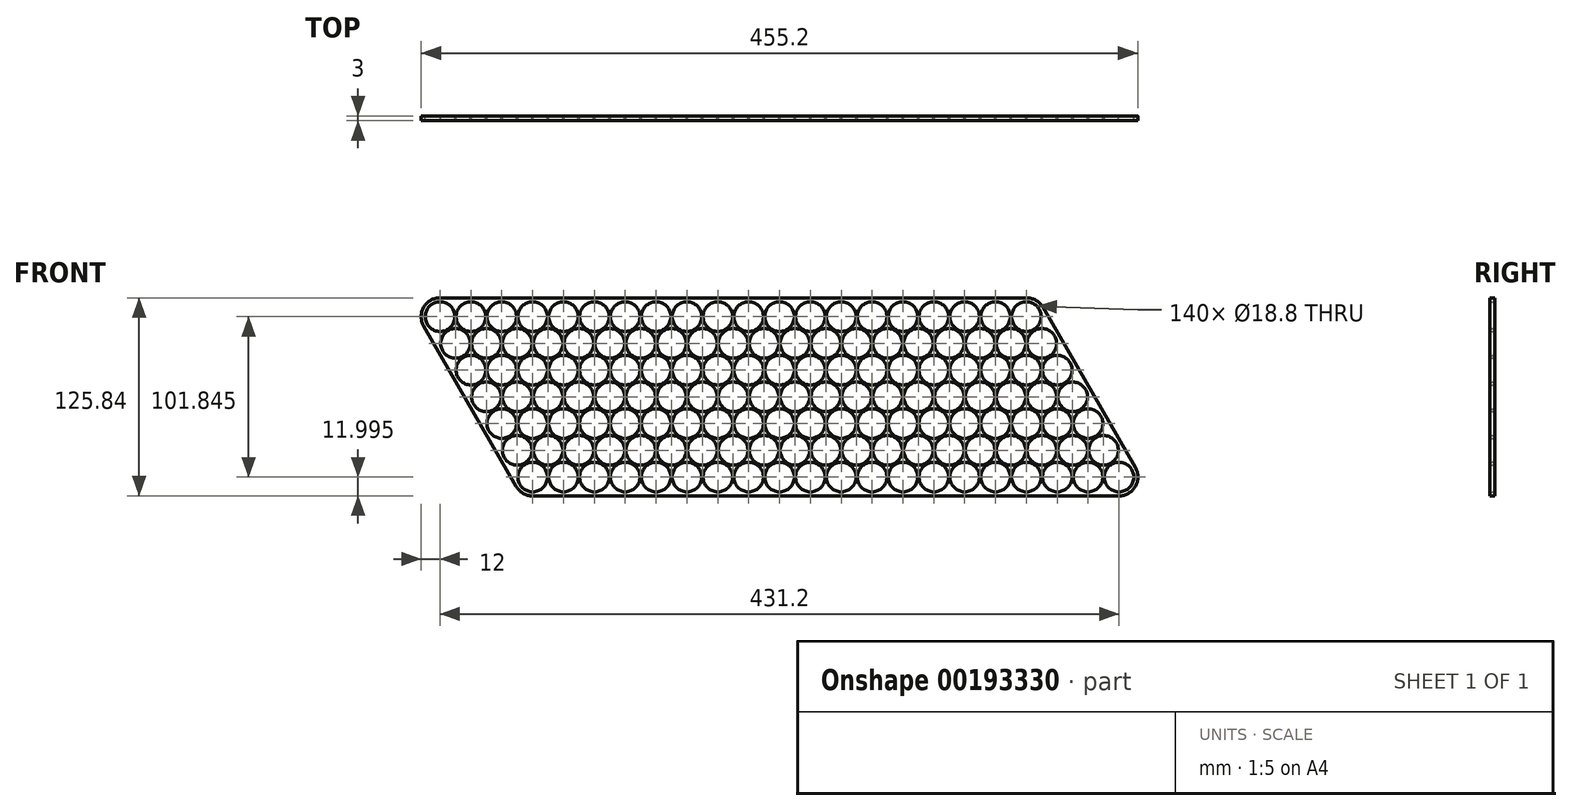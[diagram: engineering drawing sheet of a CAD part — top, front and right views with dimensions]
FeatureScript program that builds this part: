
annotation { "Feature Type Name" : "Feature", "Feature Type Description" : "" }
export const myFeature = defineFeature(function(context is Context, id is Id, definition is map)
    precondition{}
    {
        {
            var Q0;
            Q0=qCreatedBy(makeId("Front.planeOp"),FACE);
            var sketch = newSketch(context, id + "F0", { "sketchPlane" : qUnion([Q0])});
            skLineSegment(sketch, "E0", {"start": v(0, 0) * mm, "end": v(79.44, 0) * mm, "construction": true});
            skLineSegment(sketch, "E1", {"start": v(0, 0) * mm, "end": v(43.4, -75.16) * mm, "construction": true});
            skCircle(sketch, "E2", {"center": v(0, 0) * mm, "radius": 9.4 * mm});
            skCircle(sketch, "E3.1.0.0", {"center": v(19.6, 0) * mm, "radius": 9.4 * mm});
            skCircle(sketch, "E3.2.0.0", {"center": v(39.2, 0) * mm, "radius": 9.4 * mm});
            skCircle(sketch, "E3.3.0.0", {"center": v(58.8, 0) * mm, "radius": 9.4 * mm});
            skCircle(sketch, "E3.4.0.0", {"center": v(78.4, 0) * mm, "radius": 9.4 * mm});
            skCircle(sketch, "E3.5.0.0", {"center": v(98, 0) * mm, "radius": 9.4 * mm});
            skCircle(sketch, "E3.6.0.0", {"center": v(117.6, 0) * mm, "radius": 9.4 * mm});
            skCircle(sketch, "E3.7.0.0", {"center": v(137.2, 0) * mm, "radius": 9.4 * mm});
            skCircle(sketch, "E3.8.0.0", {"center": v(156.8, 0) * mm, "radius": 9.4 * mm});
            skCircle(sketch, "E3.9.0.0", {"center": v(176.4, 0) * mm, "radius": 9.4 * mm});
            skCircle(sketch, "E3.10.0.0", {"center": v(196, 0) * mm, "radius": 9.4 * mm});
            skCircle(sketch, "E3.11.0.0", {"center": v(215.6, 0) * mm, "radius": 9.4 * mm});
            skCircle(sketch, "E3.12.0.0", {"center": v(235.2, 0) * mm, "radius": 9.4 * mm});
            skCircle(sketch, "E3.13.0.0", {"center": v(254.8, 0) * mm, "radius": 9.4 * mm});
            skCircle(sketch, "E3.14.0.0", {"center": v(274.4, 0) * mm, "radius": 9.4 * mm});
            skCircle(sketch, "E3.15.0.0", {"center": v(294, 0) * mm, "radius": 9.4 * mm});
            skCircle(sketch, "E3.16.0.0", {"center": v(313.6, 0) * mm, "radius": 9.4 * mm});
            skCircle(sketch, "E3.17.0.0", {"center": v(333.2, 0) * mm, "radius": 9.4 * mm});
            skCircle(sketch, "E3.18.0.0", {"center": v(352.8, 0) * mm, "radius": 9.4 * mm});
            skCircle(sketch, "E3.19.0.0", {"center": v(372.4, 0) * mm, "radius": 9.4 * mm});
            skLineSegment(sketch, "E3.direction1", {"start": v(0, 0) * mm, "end": v(19.6, 0) * mm, "construction": true});
            skCircle(sketch, "E4.1.0.0", {"center": v(9.8, -16.97) * mm, "radius": 9.4 * mm});
            skCircle(sketch, "E4.2.0.0", {"center": v(19.6, -33.95) * mm, "radius": 9.4 * mm});
            skCircle(sketch, "E4.3.0.0", {"center": v(29.4, -50.92) * mm, "radius": 9.4 * mm});
            skCircle(sketch, "E4.4.0.0", {"center": v(39.2, -67.9) * mm, "radius": 9.4 * mm});
            skCircle(sketch, "E4.5.0.0", {"center": v(49, -84.87) * mm, "radius": 9.4 * mm});
            skCircle(sketch, "E4.6.0.0", {"center": v(58.8, -101.84) * mm, "radius": 9.4 * mm});
            skLineSegment(sketch, "E4.direction1", {"start": v(0, 0) * mm, "end": v(9.8, -16.97) * mm, "construction": true});
            skCircle(sketch, "E5.1.0.0", {"center": v(29.4, -16.97) * mm, "radius": 9.4 * mm});
            skCircle(sketch, "E5.1.0.1", {"center": v(39.2, -33.95) * mm, "radius": 9.4 * mm});
            skCircle(sketch, "E5.1.0.2", {"center": v(49, -50.92) * mm, "radius": 9.4 * mm});
            skCircle(sketch, "E5.1.0.3", {"center": v(58.8, -67.9) * mm, "radius": 9.4 * mm});
            skCircle(sketch, "E5.1.0.4", {"center": v(68.6, -84.87) * mm, "radius": 9.4 * mm});
            skCircle(sketch, "E5.1.0.5", {"center": v(78.4, -101.84) * mm, "radius": 9.4 * mm});
            skCircle(sketch, "E5.2.0.0", {"center": v(49, -16.97) * mm, "radius": 9.4 * mm});
            skCircle(sketch, "E5.2.0.1", {"center": v(58.8, -33.95) * mm, "radius": 9.4 * mm});
            skCircle(sketch, "E5.2.0.2", {"center": v(68.6, -50.92) * mm, "radius": 9.4 * mm});
            skCircle(sketch, "E5.2.0.3", {"center": v(78.4, -67.9) * mm, "radius": 9.4 * mm});
            skCircle(sketch, "E5.2.0.4", {"center": v(88.2, -84.87) * mm, "radius": 9.4 * mm});
            skCircle(sketch, "E5.2.0.5", {"center": v(98, -101.84) * mm, "radius": 9.4 * mm});
            skCircle(sketch, "E5.3.0.0", {"center": v(68.6, -16.97) * mm, "radius": 9.4 * mm});
            skCircle(sketch, "E5.3.0.1", {"center": v(78.4, -33.95) * mm, "radius": 9.4 * mm});
            skCircle(sketch, "E5.3.0.2", {"center": v(88.2, -50.92) * mm, "radius": 9.4 * mm});
            skCircle(sketch, "E5.3.0.3", {"center": v(98, -67.9) * mm, "radius": 9.4 * mm});
            skCircle(sketch, "E5.3.0.4", {"center": v(107.8, -84.87) * mm, "radius": 9.4 * mm});
            skCircle(sketch, "E5.3.0.5", {"center": v(117.6, -101.84) * mm, "radius": 9.4 * mm});
            skCircle(sketch, "E5.4.0.0", {"center": v(88.2, -16.97) * mm, "radius": 9.4 * mm});
            skCircle(sketch, "E5.4.0.1", {"center": v(98, -33.95) * mm, "radius": 9.4 * mm});
            skCircle(sketch, "E5.4.0.2", {"center": v(107.8, -50.92) * mm, "radius": 9.4 * mm});
            skCircle(sketch, "E5.4.0.3", {"center": v(117.6, -67.9) * mm, "radius": 9.4 * mm});
            skCircle(sketch, "E5.4.0.4", {"center": v(127.4, -84.87) * mm, "radius": 9.4 * mm});
            skCircle(sketch, "E5.4.0.5", {"center": v(137.2, -101.84) * mm, "radius": 9.4 * mm});
            skCircle(sketch, "E5.5.0.0", {"center": v(107.8, -16.97) * mm, "radius": 9.4 * mm});
            skCircle(sketch, "E5.5.0.1", {"center": v(117.6, -33.95) * mm, "radius": 9.4 * mm});
            skCircle(sketch, "E5.5.0.2", {"center": v(127.4, -50.92) * mm, "radius": 9.4 * mm});
            skCircle(sketch, "E5.5.0.3", {"center": v(137.2, -67.9) * mm, "radius": 9.4 * mm});
            skCircle(sketch, "E5.5.0.4", {"center": v(147, -84.87) * mm, "radius": 9.4 * mm});
            skCircle(sketch, "E5.5.0.5", {"center": v(156.8, -101.84) * mm, "radius": 9.4 * mm});
            skCircle(sketch, "E5.6.0.0", {"center": v(127.4, -16.97) * mm, "radius": 9.4 * mm});
            skCircle(sketch, "E5.6.0.1", {"center": v(137.2, -33.95) * mm, "radius": 9.4 * mm});
            skCircle(sketch, "E5.6.0.2", {"center": v(147, -50.92) * mm, "radius": 9.4 * mm});
            skCircle(sketch, "E5.6.0.3", {"center": v(156.8, -67.9) * mm, "radius": 9.4 * mm});
            skCircle(sketch, "E5.6.0.4", {"center": v(166.6, -84.87) * mm, "radius": 9.4 * mm});
            skCircle(sketch, "E5.6.0.5", {"center": v(176.4, -101.84) * mm, "radius": 9.4 * mm});
            skCircle(sketch, "E5.7.0.0", {"center": v(147, -16.97) * mm, "radius": 9.4 * mm});
            skCircle(sketch, "E5.7.0.1", {"center": v(156.8, -33.95) * mm, "radius": 9.4 * mm});
            skCircle(sketch, "E5.7.0.2", {"center": v(166.6, -50.92) * mm, "radius": 9.4 * mm});
            skCircle(sketch, "E5.7.0.3", {"center": v(176.4, -67.9) * mm, "radius": 9.4 * mm});
            skCircle(sketch, "E5.7.0.4", {"center": v(186.2, -84.87) * mm, "radius": 9.4 * mm});
            skCircle(sketch, "E5.7.0.5", {"center": v(196, -101.84) * mm, "radius": 9.4 * mm});
            skCircle(sketch, "E5.8.0.0", {"center": v(166.6, -16.97) * mm, "radius": 9.4 * mm});
            skCircle(sketch, "E5.8.0.1", {"center": v(176.4, -33.95) * mm, "radius": 9.4 * mm});
            skCircle(sketch, "E5.8.0.2", {"center": v(186.2, -50.92) * mm, "radius": 9.4 * mm});
            skCircle(sketch, "E5.8.0.3", {"center": v(196, -67.9) * mm, "radius": 9.4 * mm});
            skCircle(sketch, "E5.8.0.4", {"center": v(205.8, -84.87) * mm, "radius": 9.4 * mm});
            skCircle(sketch, "E5.8.0.5", {"center": v(215.6, -101.84) * mm, "radius": 9.4 * mm});
            skCircle(sketch, "E5.9.0.0", {"center": v(186.2, -16.97) * mm, "radius": 9.4 * mm});
            skCircle(sketch, "E5.9.0.1", {"center": v(196, -33.95) * mm, "radius": 9.4 * mm});
            skCircle(sketch, "E5.9.0.2", {"center": v(205.8, -50.92) * mm, "radius": 9.4 * mm});
            skCircle(sketch, "E5.9.0.3", {"center": v(215.6, -67.9) * mm, "radius": 9.4 * mm});
            skCircle(sketch, "E5.9.0.4", {"center": v(225.4, -84.87) * mm, "radius": 9.4 * mm});
            skCircle(sketch, "E5.9.0.5", {"center": v(235.2, -101.84) * mm, "radius": 9.4 * mm});
            skCircle(sketch, "E5.10.0.0", {"center": v(205.8, -16.97) * mm, "radius": 9.4 * mm});
            skCircle(sketch, "E5.10.0.1", {"center": v(215.6, -33.95) * mm, "radius": 9.4 * mm});
            skCircle(sketch, "E5.10.0.2", {"center": v(225.4, -50.92) * mm, "radius": 9.4 * mm});
            skCircle(sketch, "E5.10.0.3", {"center": v(235.2, -67.9) * mm, "radius": 9.4 * mm});
            skCircle(sketch, "E5.10.0.4", {"center": v(245, -84.87) * mm, "radius": 9.4 * mm});
            skCircle(sketch, "E5.10.0.5", {"center": v(254.8, -101.84) * mm, "radius": 9.4 * mm});
            skCircle(sketch, "E5.11.0.0", {"center": v(225.4, -16.97) * mm, "radius": 9.4 * mm});
            skCircle(sketch, "E5.11.0.1", {"center": v(235.2, -33.95) * mm, "radius": 9.4 * mm});
            skCircle(sketch, "E5.11.0.2", {"center": v(245, -50.92) * mm, "radius": 9.4 * mm});
            skCircle(sketch, "E5.11.0.3", {"center": v(254.8, -67.9) * mm, "radius": 9.4 * mm});
            skCircle(sketch, "E5.11.0.4", {"center": v(264.6, -84.87) * mm, "radius": 9.4 * mm});
            skCircle(sketch, "E5.11.0.5", {"center": v(274.4, -101.84) * mm, "radius": 9.4 * mm});
            skCircle(sketch, "E5.12.0.0", {"center": v(245, -16.97) * mm, "radius": 9.4 * mm});
            skCircle(sketch, "E5.12.0.1", {"center": v(254.8, -33.95) * mm, "radius": 9.4 * mm});
            skCircle(sketch, "E5.12.0.2", {"center": v(264.6, -50.92) * mm, "radius": 9.4 * mm});
            skCircle(sketch, "E5.12.0.3", {"center": v(274.4, -67.9) * mm, "radius": 9.4 * mm});
            skCircle(sketch, "E5.12.0.4", {"center": v(284.2, -84.87) * mm, "radius": 9.4 * mm});
            skCircle(sketch, "E5.12.0.5", {"center": v(294, -101.84) * mm, "radius": 9.4 * mm});
            skCircle(sketch, "E5.13.0.0", {"center": v(264.6, -16.97) * mm, "radius": 9.4 * mm});
            skCircle(sketch, "E5.13.0.1", {"center": v(274.4, -33.95) * mm, "radius": 9.4 * mm});
            skCircle(sketch, "E5.13.0.2", {"center": v(284.2, -50.92) * mm, "radius": 9.4 * mm});
            skCircle(sketch, "E5.13.0.3", {"center": v(294, -67.9) * mm, "radius": 9.4 * mm});
            skCircle(sketch, "E5.13.0.4", {"center": v(303.8, -84.87) * mm, "radius": 9.4 * mm});
            skCircle(sketch, "E5.13.0.5", {"center": v(313.6, -101.84) * mm, "radius": 9.4 * mm});
            skCircle(sketch, "E5.14.0.0", {"center": v(284.2, -16.97) * mm, "radius": 9.4 * mm});
            skCircle(sketch, "E5.14.0.1", {"center": v(294, -33.95) * mm, "radius": 9.4 * mm});
            skCircle(sketch, "E5.14.0.2", {"center": v(303.8, -50.92) * mm, "radius": 9.4 * mm});
            skCircle(sketch, "E5.14.0.3", {"center": v(313.6, -67.9) * mm, "radius": 9.4 * mm});
            skCircle(sketch, "E5.14.0.4", {"center": v(323.4, -84.87) * mm, "radius": 9.4 * mm});
            skCircle(sketch, "E5.14.0.5", {"center": v(333.2, -101.84) * mm, "radius": 9.4 * mm});
            skCircle(sketch, "E5.15.0.0", {"center": v(303.8, -16.97) * mm, "radius": 9.4 * mm});
            skCircle(sketch, "E5.15.0.1", {"center": v(313.6, -33.95) * mm, "radius": 9.4 * mm});
            skCircle(sketch, "E5.15.0.2", {"center": v(323.4, -50.92) * mm, "radius": 9.4 * mm});
            skCircle(sketch, "E5.15.0.3", {"center": v(333.2, -67.9) * mm, "radius": 9.4 * mm});
            skCircle(sketch, "E5.15.0.4", {"center": v(343, -84.87) * mm, "radius": 9.4 * mm});
            skCircle(sketch, "E5.15.0.5", {"center": v(352.8, -101.84) * mm, "radius": 9.4 * mm});
            skCircle(sketch, "E5.16.0.0", {"center": v(323.4, -16.97) * mm, "radius": 9.4 * mm});
            skCircle(sketch, "E5.16.0.1", {"center": v(333.2, -33.95) * mm, "radius": 9.4 * mm});
            skCircle(sketch, "E5.16.0.2", {"center": v(343, -50.92) * mm, "radius": 9.4 * mm});
            skCircle(sketch, "E5.16.0.3", {"center": v(352.8, -67.9) * mm, "radius": 9.4 * mm});
            skCircle(sketch, "E5.16.0.4", {"center": v(362.6, -84.87) * mm, "radius": 9.4 * mm});
            skCircle(sketch, "E5.16.0.5", {"center": v(372.4, -101.84) * mm, "radius": 9.4 * mm});
            skCircle(sketch, "E5.17.0.0", {"center": v(343, -16.97) * mm, "radius": 9.4 * mm});
            skCircle(sketch, "E5.17.0.1", {"center": v(352.8, -33.95) * mm, "radius": 9.4 * mm});
            skCircle(sketch, "E5.17.0.2", {"center": v(362.6, -50.92) * mm, "radius": 9.4 * mm});
            skCircle(sketch, "E5.17.0.3", {"center": v(372.4, -67.9) * mm, "radius": 9.4 * mm});
            skCircle(sketch, "E5.17.0.4", {"center": v(382.2, -84.87) * mm, "radius": 9.4 * mm});
            skCircle(sketch, "E5.17.0.5", {"center": v(392, -101.84) * mm, "radius": 9.4 * mm});
            skCircle(sketch, "E5.18.0.0", {"center": v(362.6, -16.97) * mm, "radius": 9.4 * mm});
            skCircle(sketch, "E5.18.0.1", {"center": v(372.4, -33.95) * mm, "radius": 9.4 * mm});
            skCircle(sketch, "E5.18.0.2", {"center": v(382.2, -50.92) * mm, "radius": 9.4 * mm});
            skCircle(sketch, "E5.18.0.3", {"center": v(392, -67.9) * mm, "radius": 9.4 * mm});
            skCircle(sketch, "E5.18.0.4", {"center": v(401.8, -84.87) * mm, "radius": 9.4 * mm});
            skCircle(sketch, "E5.18.0.5", {"center": v(411.6, -101.84) * mm, "radius": 9.4 * mm});
            skCircle(sketch, "E5.19.0.0", {"center": v(382.2, -16.97) * mm, "radius": 9.4 * mm});
            skCircle(sketch, "E5.19.0.1", {"center": v(392, -33.95) * mm, "radius": 9.4 * mm});
            skCircle(sketch, "E5.19.0.2", {"center": v(401.8, -50.92) * mm, "radius": 9.4 * mm});
            skCircle(sketch, "E5.19.0.3", {"center": v(411.6, -67.9) * mm, "radius": 9.4 * mm});
            skCircle(sketch, "E5.19.0.4", {"center": v(421.4, -84.87) * mm, "radius": 9.4 * mm});
            skCircle(sketch, "E5.19.0.5", {"center": v(431.2, -101.84) * mm, "radius": 9.4 * mm});
            skLineSegment(sketch, "E5.direction1", {"start": v(9.8, -16.97) * mm, "end": v(29.4, -16.97) * mm, "construction": true});
            skLineSegment(sketch, "E6", {"start": v(0, 0) * mm, "end": v(372.4, 0) * mm, "construction": true});
            skLineSegment(sketch, "E7", {"start": v(372.4, 0) * mm, "end": v(441, -118.82) * mm, "construction": true});
            skLineSegment(sketch, "E8", {"start": v(441, -118.82) * mm, "end": v(68.6, -118.82) * mm, "construction": true});
            skLineSegment(sketch, "E9", {"start": v(68.6, -118.82) * mm, "end": v(0, 0) * mm, "construction": true});
            skArc(sketch, "E10", {"start": v(48.4, -107.84) * mm, "mid": v(52.8, -112.24) * mm, "end": v(58.8, -113.84) * mm});
            skArc(sketch, "E11", {"start": v(431.2, -113.84) * mm, "mid": v(441.6, -107.84) * mm, "end": v(441.6, -95.84) * mm});
            skArc(sketch, "E12", {"start": v(382.8, 6) * mm, "mid": v(378.4, 10.4) * mm, "end": v(372.4, 12) * mm});
            skArc(sketch, "E13", {"start": v(0, 12) * mm, "mid": v(-10.4, 6) * mm, "end": v(-10.4, -6) * mm});
            skLineSegment(sketch, "E14", {"start": v(0, 12) * mm, "end": v(372.4, 12) * mm});
            skLineSegment(sketch, "E15", {"start": v(-10.4, -6) * mm, "end": v(48.4, -107.84) * mm});
            skLineSegment(sketch, "E16", {"start": v(58.8, -113.84) * mm, "end": v(431.2, -113.84) * mm});
            skLineSegment(sketch, "E17", {"start": v(441.6, -95.84) * mm, "end": v(382.8, 6) * mm});
            skLineSegment(sketch, "E18", {"start": v(441.6, -107.84) * mm, "end": v(500.4, -6) * mm, "construction": true});
            skLineSegment(sketch, "E19", {"start": v(372.4, 12) * mm, "end": v(490, 12) * mm, "construction": true});
            skPoint(sketch, "E20.visualSharp", {"position": v(510.78, 12) * mm});
            skArc(sketch, "E20.filletArc", {"start": v(500.4, -6) * mm, "mid": v(500.4, 6) * mm, "end": v(490, 12) * mm, "construction": true});
            skSolve(sketch);
        }
        {
            var Q0;
            Q0=makeQuery(id+"F0.imprint","IMPRINT",FACE,{"disambiguationData":[TD([[makeQuery(id+"F0.imprint","IMPRINT",EDGE,{"derivedFrom":sQuery(id+"F0.wireOp",EDGE,"E2")}),-1.0]])]});
            extrude(context, id + "F1", {"entities" : qUnion([Q0]), "depth" : 3 * mm});
        }
    });
